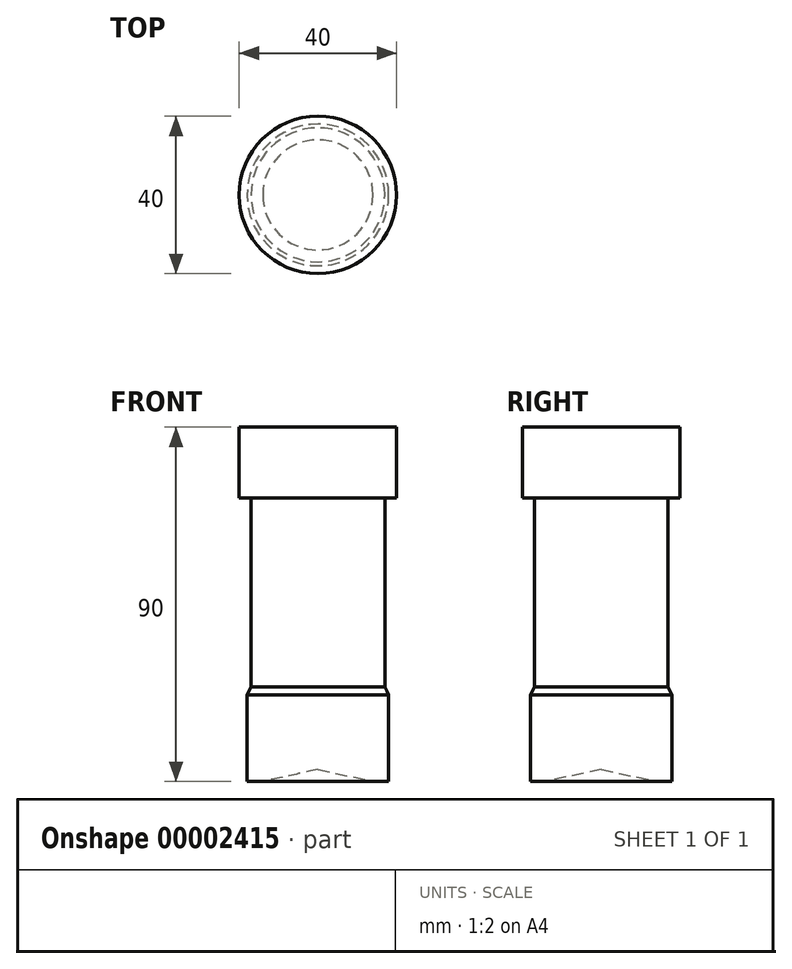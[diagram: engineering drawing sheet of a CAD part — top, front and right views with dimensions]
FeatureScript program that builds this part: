
annotation { "Feature Type Name" : "Feature", "Feature Type Description" : "" }
export const myFeature = defineFeature(function(context is Context, id is Id, definition is map)
    precondition{}
    {
        {
            var Q0;
            Q0=qCreatedBy(makeId("Front.planeOp"),FACE);
            var sketch = newSketch(context, id + "F0", { "sketchPlane" : qUnion([Q0])});
            skLineSegment(sketch, "E0", {"start": v(-27.99, 68.14) * mm, "end": v(-27.99, -51.86) * mm, "construction": true});
            skLineSegment(sketch, "E1", {"start": v(-27.99, -33.86) * mm, "end": v(-41.99, -36.86) * mm});
            skLineSegment(sketch, "E2", {"start": v(-41.99, -36.86) * mm, "end": v(-45.99, -36.86) * mm});
            skLineSegment(sketch, "E3", {"start": v(-45.99, -36.86) * mm, "end": v(-45.99, -14.86) * mm});
            skLineSegment(sketch, "E4", {"start": v(-45.99, -14.86) * mm, "end": v(-44.99, -12.86) * mm});
            skLineSegment(sketch, "E5", {"start": v(-44.99, -12.86) * mm, "end": v(-44.99, 35.14) * mm});
            skLineSegment(sketch, "E6", {"start": v(-44.99, 35.14) * mm, "end": v(-47.99, 35.14) * mm});
            skLineSegment(sketch, "E7", {"start": v(-47.99, 35.14) * mm, "end": v(-47.99, 53.14) * mm});
            skLineSegment(sketch, "E8", {"start": v(-47.99, 53.14) * mm, "end": v(-27.99, 53.14) * mm});
            skLineSegment(sketch, "E9", {"start": v(-27.99, 53.14) * mm, "end": v(-27.99, -33.86) * mm});
            skSolve(sketch);
        }
        {
            var Q0;
            Q0=makeQuery(id+"F0.imprint","IMPRINT",FACE,{"disambiguationData":[TD([[makeQuery(id+"F0.imprint","IMPRINT",EDGE,{"derivedFrom":sQuery(id+"F0.wireOp",EDGE,"E1")}),-1.0]])]});
            var Q1;
            Q1=sQuery(id+"F0.wireOp",EDGE,"E0");
            revolve(context, id + "F1", {"entities" : qUnion([Q0]), "axis" : qUnion([Q1]), "revolveType" : RevolveType.FULL});
        }
    });
